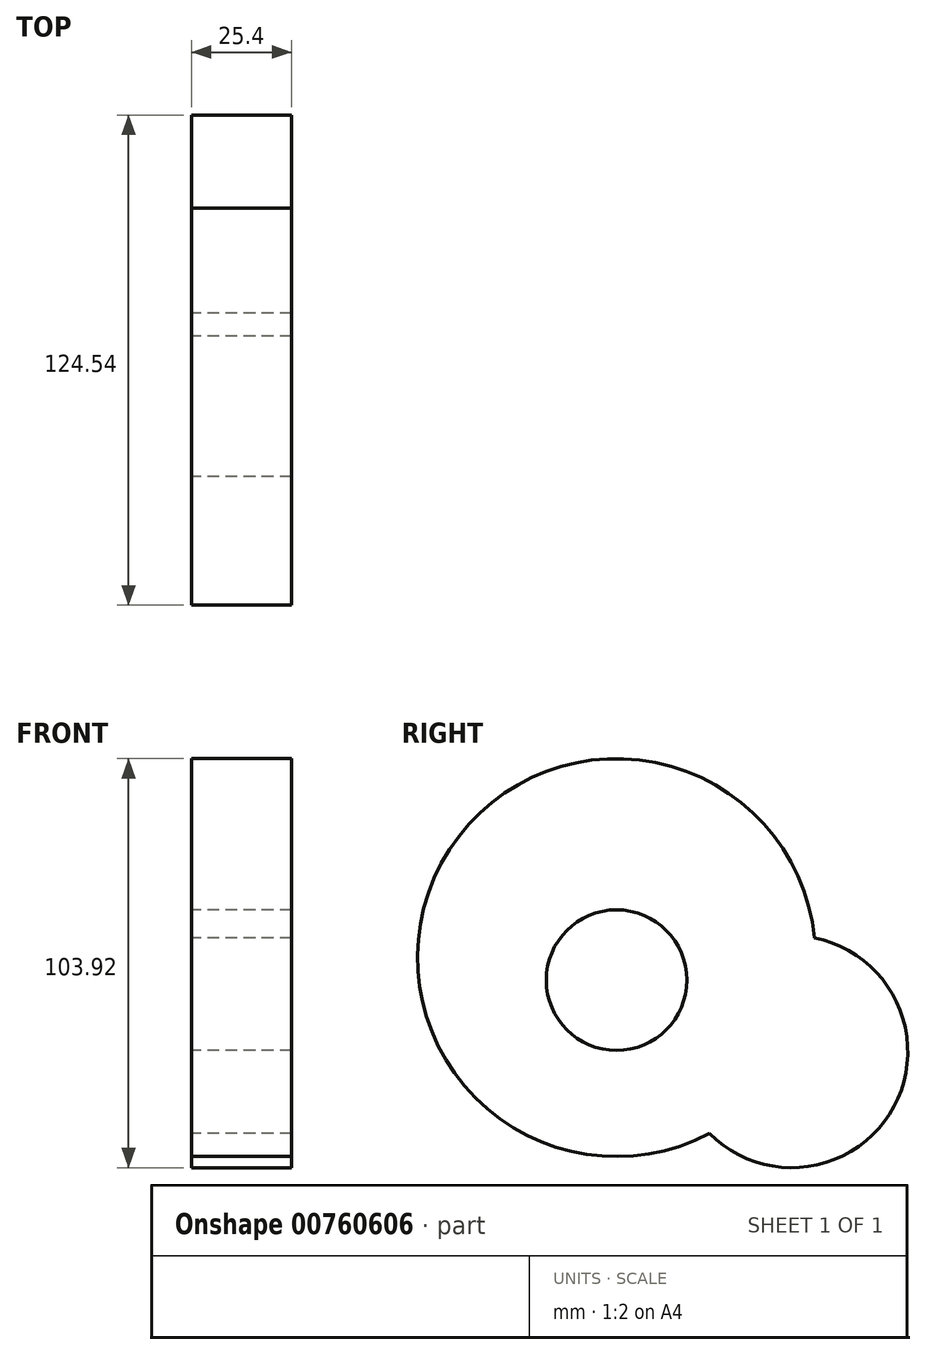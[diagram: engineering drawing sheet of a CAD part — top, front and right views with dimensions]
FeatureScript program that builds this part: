
annotation { "Feature Type Name" : "Feature", "Feature Type Description" : "" }
export const myFeature = defineFeature(function(context is Context, id is Id, definition is map)
    precondition{}
    {
        {
            var Q0;
            Q0=qCreatedBy(makeId("Right.planeOp"),FACE);
            var sketch = newSketch(context, id + "F0", { "sketchPlane" : qUnion([Q0])});
            skCircle(sketch, "E0", {"center": v(0, 39.3) * mm, "radius": 50.54 * mm});
            skCircle(sketch, "E1", {"center": v(0, 33.59) * mm, "radius": 17.86 * mm});
            skCircle(sketch, "E2", {"center": v(44.53, 15.4) * mm, "radius": 29.47 * mm});
            skSolve(sketch);
        }
        {
            var Q0;
            Q0 = qSketchRegion(id + "F0", true);
            extrude(context, id + "F1", {"entities" : qUnion([Q0]), "depth" : 25.4 * mm, "offsetDistance" : 25.4 * mm});
        }
    });
